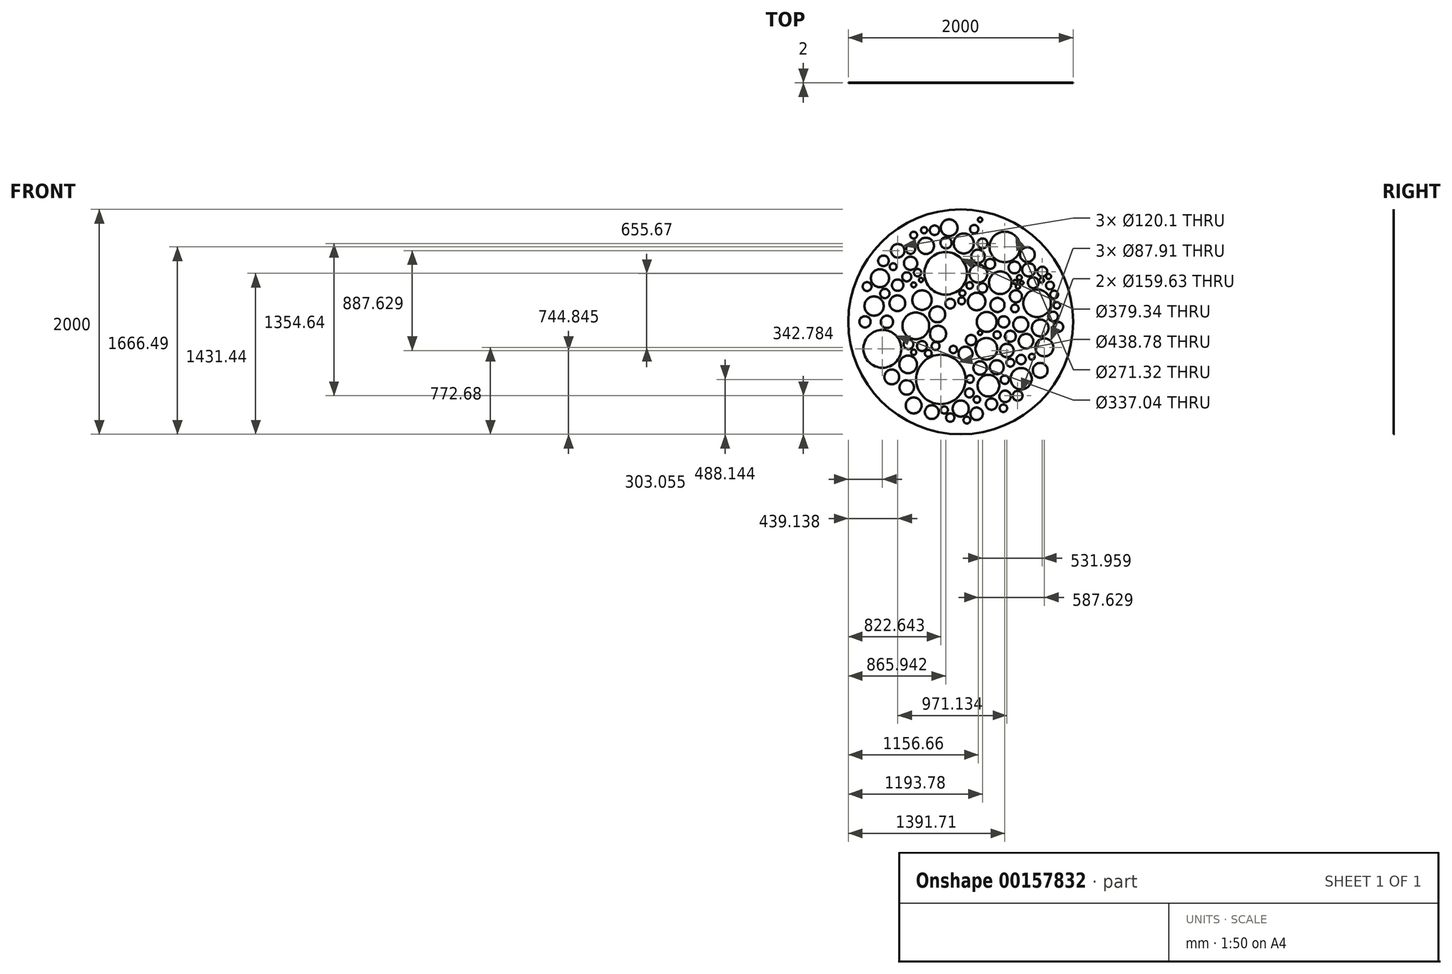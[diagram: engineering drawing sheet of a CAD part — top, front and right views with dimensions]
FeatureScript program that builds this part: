
annotation { "Feature Type Name" : "Feature", "Feature Type Description" : "" }
export const myFeature = defineFeature(function(context is Context, id is Id, definition is map)
    precondition{}
    {
        {
            var Q0;
            Q0=qCreatedBy(makeId("Front.planeOp"),FACE);
            var sketch = newSketch(context, id + "F0", { "sketchPlane" : qUnion([Q0])});
            skCircle(sketch, "E0", {"center": v(0, 0) * mm, "radius": 1000 * mm});
            skCircle(sketch, "E1", {"center": v(0, 0) * mm, "radius": 121.83 * mm, "construction": true});
            skCircle(sketch, "E2", {"center": v(141.2, 180.93) * mm, "radius": 78.06 * mm});
            skCircle(sketch, "E3", {"center": v(230.9, 0) * mm, "radius": 88.36 * mm});
            skCircle(sketch, "E4", {"center": v(-134.06, 431.44) * mm, "radius": 189.67 * mm});
            skCircle(sketch, "E5", {"center": v(-344.37, 193.3) * mm, "radius": 86.65 * mm});
            skCircle(sketch, "E6", {"center": v(-400.04, -35.57) * mm, "radius": 119.02 * mm});
            skCircle(sketch, "E7", {"center": v(-208.28, 66.5) * mm, "radius": 70.6 * mm});
            skCircle(sketch, "E8", {"center": v(-93.85, 162.37) * mm, "radius": 43.4 * mm});
            skCircle(sketch, "E9", {"center": v(156.66, 428.35) * mm, "radius": 79.82 * mm});
            skCircle(sketch, "E10", {"center": v(351.5, 347.94) * mm, "radius": 100.36 * mm});
            skCircle(sketch, "E11", {"center": v(326.77, 150) * mm, "radius": 62.87 * mm});
            skCircle(sketch, "E12", {"center": v(-177.36, -511.86) * mm, "radius": 219.4 * mm});
            skCircle(sketch, "E13", {"center": v(246.35, -567.53) * mm, "radius": 96.22 * mm});
            skCircle(sketch, "E14", {"center": v(227.8, -239.7) * mm, "radius": 96.32 * mm});
            skCircle(sketch, "E15", {"center": v(441.2, -128.35) * mm, "radius": 48.9 * mm});
            skCircle(sketch, "E16", {"center": v(323.67, -115.98) * mm, "radius": 32.29 * mm});
            skCircle(sketch, "E17", {"center": v(382.44, 0) * mm, "radius": 49.8 * mm});
            skCircle(sketch, "E18", {"center": v(481.4, 119.07) * mm, "radius": 34.16 * mm});
            skCircle(sketch, "E19", {"center": v(490.68, 227.32) * mm, "radius": 54.01 * mm});
            skCircle(sketch, "E20", {"center": v(533.98, -23.2) * mm, "radius": 66.5 * mm});
            skCircle(sketch, "E21", {"center": v(679.34, 165.46) * mm, "radius": 122.78 * mm});
            skCircle(sketch, "E22", {"center": v(707.18, -54.12) * mm, "radius": 74.36 * mm});
            skCircle(sketch, "E23", {"center": v(580.37, -171.65) * mm, "radius": 64.58 * mm});
            skCircle(sketch, "E24", {"center": v(410.27, -255.15) * mm, "radius": 60.05 * mm});
            skCircle(sketch, "E25", {"center": v(537.08, -335.57) * mm, "radius": 41.5 * mm});
            skCircle(sketch, "E26", {"center": v(632.95, -310.82) * mm, "radius": 26.24 * mm});
            skCircle(sketch, "E27", {"center": v(441.2, -363.4) * mm, "radius": 35.26 * mm});
            skCircle(sketch, "E28", {"center": v(744.3, -227.32) * mm, "radius": 79.82 * mm});
            skCircle(sketch, "E29", {"center": v(537.08, -505.67) * mm, "radius": 94.67 * mm});
            skCircle(sketch, "E30", {"center": v(707.18, -431.44) * mm, "radius": 65.75 * mm});
            skCircle(sketch, "E31", {"center": v(-202.1, -106.7) * mm, "radius": 71.94 * mm});
            skCircle(sketch, "E32", {"center": v(-66.02, -245.88) * mm, "radius": 32.88 * mm});
            skCircle(sketch, "E33", {"center": v(-464.99, -199.48) * mm, "radius": 42.97 * mm});
            skCircle(sketch, "E34", {"center": v(-344.37, -214.95) * mm, "radius": 44.6 * mm});
            skCircle(sketch, "E35", {"center": v(-601.07, 490.2) * mm, "radius": 30.62 * mm});
            skCircle(sketch, "E36", {"center": v(-446.43, 644.85) * mm, "radius": 40.32 * mm});
            skCircle(sketch, "E37", {"center": v(-103.13, 836.6) * mm, "radius": 74.8 * mm});
            skCircle(sketch, "E38", {"center": v(193.78, 697.42) * mm, "radius": 43.96 * mm});
            skCircle(sketch, "E39", {"center": v(172.13, 907.73) * mm, "radius": 19.8 * mm});
            skCircle(sketch, "E40", {"center": v(-771.17, 140.72) * mm, "radius": 85.32 * mm});
            skCircle(sketch, "E41", {"center": v(0, 0) * mm, "radius": 932.92 * mm, "construction": true});
            skCircle(sketch, "E42", {"center": v(119.55, 824.23) * mm, "radius": 37.24 * mm});
            skCircle(sketch, "E43", {"center": v(391.72, 666.5) * mm, "radius": 135.66 * mm});
            skCircle(sketch, "E44", {"center": v(-696.94, -239.7) * mm, "radius": 168.52 * mm});
            skCircle(sketch, "E45", {"center": v(-468.08, -378.87) * mm, "radius": 78.85 * mm});
            skCircle(sketch, "E46", {"center": v(42.23, -282.99) * mm, "radius": 62.24 * mm});
            skCircle(sketch, "E47", {"center": v(91.72, -162.37) * mm, "radius": 45.66 * mm});
            skCircle(sketch, "E48", {"center": v(172.13, -409.8) * mm, "radius": 59.5 * mm});
            skCircle(sketch, "E49", {"center": v(320.58, -403.6) * mm, "radius": 61.86 * mm});
            skCircle(sketch, "E50", {"center": v(82.44, -508.76) * mm, "radius": 33.45 * mm});
            skCircle(sketch, "E51", {"center": v(76.25, -632.47) * mm, "radius": 39.36 * mm});
            skCircle(sketch, "E52", {"center": v(144.3, -691.24) * mm, "radius": 29.18 * mm});
            skCircle(sketch, "E53", {"center": v(0, -771.65) * mm, "radius": 71.79 * mm});
            skCircle(sketch, "E54", {"center": v(141.2, -818.04) * mm, "radius": 55.76 * mm});
            skCircle(sketch, "E55", {"center": v(274.19, -731.44) * mm, "radius": 50.73 * mm});
            skCircle(sketch, "E56", {"center": v(394.8, -663.4) * mm, "radius": 51.2 * mm});
            skCircle(sketch, "E57", {"center": v(391.72, -514.95) * mm, "radius": 37.24 * mm});
            skCircle(sketch, "E58", {"center": v(506.15, -657.22) * mm, "radius": 43.96 * mm});
            skCircle(sketch, "E59", {"center": v(379.34, -768.56) * mm, "radius": 33.45 * mm});
            skCircle(sketch, "E60", {"center": v(-560.86, 326.29) * mm, "radius": 50.73 * mm});
            skCircle(sketch, "E61", {"center": v(-480.45, 400.52) * mm, "radius": 40.2 * mm});
            skCircle(sketch, "E62", {"center": v(-446.43, 521.13) * mm, "radius": 59.41 * mm});
            skCircle(sketch, "E63", {"center": v(-310.35, 675.77) * mm, "radius": 72.2 * mm});
            skCircle(sketch, "E64", {"center": v(-130.97, 703.6) * mm, "radius": 49.87 * mm});
            skCircle(sketch, "E65", {"center": v(26.77, 697.42) * mm, "radius": 89.2 * mm});
            skCircle(sketch, "E66", {"center": v(153.57, 582.99) * mm, "radius": 60.05 * mm});
            skCircle(sketch, "E67", {"center": v(261.82, 514.95) * mm, "radius": 44.6 * mm});
            skCircle(sketch, "E68", {"center": v(478.31, 484.02) * mm, "radius": 52.58 * mm});
            skCircle(sketch, "E69", {"center": v(592.75, 598.45) * mm, "radius": 65.6 * mm});
            skCircle(sketch, "E70", {"center": v(605.12, 462.37) * mm, "radius": 58.35 * mm});
            skCircle(sketch, "E71", {"center": v(521.61, 394.33) * mm, "radius": 21.65 * mm});
            skCircle(sketch, "E72", {"center": v(484.5, 354.12) * mm, "radius": 19.56 * mm});
            skCircle(sketch, "E73", {"center": v(543.26, 347.94) * mm, "radius": 15.77 * mm});
            skCircle(sketch, "E74", {"center": v(509.24, 313.92) * mm, "radius": 19.56 * mm});
            skCircle(sketch, "E75", {"center": v(645.32, 347.94) * mm, "radius": 48.01 * mm});
            skCircle(sketch, "E76", {"center": v(172.13, -97.42) * mm, "radius": 18.81 * mm});
            skCircle(sketch, "E77", {"center": v(79.34, 323.2) * mm, "radius": 29.18 * mm});
            skCircle(sketch, "E78", {"center": v(14.4, 255.15) * mm, "radius": 26.6 * mm});
            skCircle(sketch, "E79", {"center": v(8.2, 187.11) * mm, "radius": 30.93 * mm});
            skCircle(sketch, "E80", {"center": v(193.78, 301.55) * mm, "radius": 42.07 * mm});
            skCircle(sketch, "E81", {"center": v(725.74, 446.9) * mm, "radius": 43.96 * mm});
            skCircle(sketch, "E82", {"center": v(793.78, 323.2) * mm, "radius": 35 * mm});
            skCircle(sketch, "E83", {"center": v(719.55, 369.59) * mm, "radius": 20.75 * mm});
            skCircle(sketch, "E84", {"center": v(781.4, 403.6) * mm, "radius": 22.52 * mm});
            skCircle(sketch, "E85", {"center": v(830.9, 242.78) * mm, "radius": 35.26 * mm});
            skCircle(sketch, "E86", {"center": v(855.63, 146.9) * mm, "radius": 29.34 * mm});
            skCircle(sketch, "E87", {"center": v(821.61, 47.94) * mm, "radius": 42.97 * mm});
            skCircle(sketch, "E88", {"center": v(868, -44.85) * mm, "radius": 43.74 * mm});
            skCircle(sketch, "E89", {"center": v(-223.75, -214.95) * mm, "radius": 35.26 * mm});
            skCircle(sketch, "E90", {"center": v(-288.7, -279.9) * mm, "radius": 30.46 * mm});
            skCircle(sketch, "E91", {"center": v(-418.6, -270.62) * mm, "radius": 23.55 * mm});
            skCircle(sketch, "E92", {"center": v(-563.95, 165.46) * mm, "radius": 70.12 * mm});
            skCircle(sketch, "E93", {"center": v(-418.6, 329.38) * mm, "radius": 22.3 * mm});
            skCircle(sketch, "E94", {"center": v(-384.57, 437.63) * mm, "radius": 32.88 * mm});
            skCircle(sketch, "E95", {"center": v(-353.65, 372.68) * mm, "radius": 18.56 * mm});
            skCircle(sketch, "E96", {"center": v(-718.6, 388.14) * mm, "radius": 80.41 * mm});
            skCircle(sketch, "E97", {"center": v(-560.86, 632.47) * mm, "radius": 60.05 * mm});
            skCircle(sketch, "E98", {"center": v(-656.74, 0) * mm, "radius": 54.91 * mm});
            skCircle(sketch, "E99", {"center": v(-613.44, -490.2) * mm, "radius": 65.75 * mm});
            skCircle(sketch, "E100", {"center": v(-480.45, -582.99) * mm, "radius": 64.36 * mm});
            skCircle(sketch, "E101", {"center": v(-418.6, -743.81) * mm, "radius": 70.53 * mm});
            skCircle(sketch, "E102", {"center": v(-257.77, -802.58) * mm, "radius": 61.39 * mm});
            skCircle(sketch, "E103", {"center": v(-146.43, -784.02) * mm, "radius": 31.84 * mm});
            skCircle(sketch, "E104", {"center": v(-93.85, -852.06) * mm, "radius": 37.24 * mm});
            skCircle(sketch, "E105", {"center": v(54.6, -873.71) * mm, "radius": 30.46 * mm});
            skCircle(sketch, "E106", {"center": v(-851.58, 0) * mm, "radius": 50.18 * mm});
            skCircle(sketch, "E107", {"center": v(-675.3, 252.06) * mm, "radius": 41.5 * mm});
            skCircle(sketch, "E108", {"center": v(-833.03, 313.92) * mm, "radius": 39.6 * mm});
            skCircle(sketch, "E109", {"center": v(-687.67, 542.78) * mm, "radius": 47.1 * mm});
            skCircle(sketch, "E110", {"center": v(-418.6, 771.65) * mm, "radius": 30.62 * mm});
            skCircle(sketch, "E111", {"center": v(-325.81, 814.95) * mm, "radius": 27.66 * mm});
            skCircle(sketch, "E112", {"center": v(-233.03, 814.95) * mm, "radius": 42.07 * mm});
            skSolve(sketch);
        }
        {
            var Q0;
            Q0=makeQuery(id+"F0.imprint","IMPRINT",FACE,{"disambiguationData":[TD([[makeQuery(id+"F0.imprint","IMPRINT",EDGE,{"derivedFrom":sQuery(id+"F0.wireOp",EDGE,"E0")}),1.0]])]});
            extrude(context, id + "F1", {"entities" : qUnion([Q0]), "depth" : 2 * mm});
        }
    });
